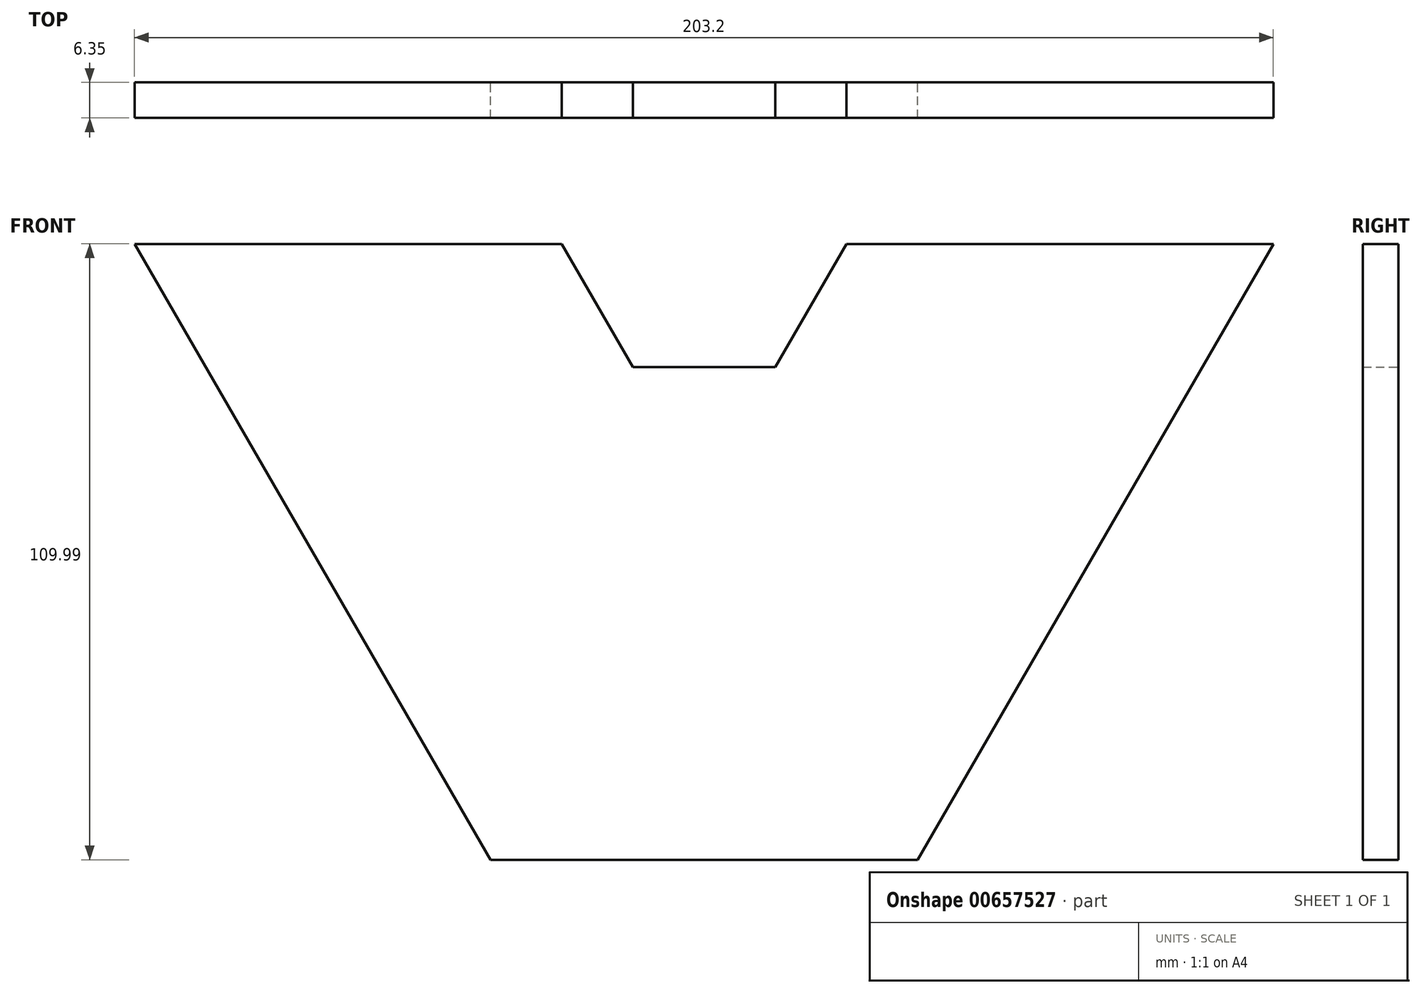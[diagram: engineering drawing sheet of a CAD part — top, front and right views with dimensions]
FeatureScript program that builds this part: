
annotation { "Feature Type Name" : "Feature", "Feature Type Description" : "" }
export const myFeature = defineFeature(function(context is Context, id is Id, definition is map)
    precondition{}
    {
        {
            var Q0;
            Q0=qCreatedBy(makeId("Front.planeOp"),FACE);
            var sketch = newSketch(context, id + "F0", { "sketchPlane" : qUnion([Q0])});
            skLineSegment(sketch, "E0", {"start": v(-34.47, 0) * mm, "end": v(41.73, 0) * mm});
            skLineSegment(sketch, "E1", {"start": v(41.73, 0) * mm, "end": v(105.23, 109.99) * mm});
            skLineSegment(sketch, "E2", {"start": v(105.23, 109.99) * mm, "end": v(29.03, 109.99) * mm});
            skLineSegment(sketch, "E3", {"start": v(29.03, 109.99) * mm, "end": v(16.33, 87.99) * mm});
            skLineSegment(sketch, "E4", {"start": v(16.33, 87.99) * mm, "end": v(-9.07, 87.99) * mm});
            skLineSegment(sketch, "E5", {"start": v(-9.07, 87.99) * mm, "end": v(-21.77, 109.99) * mm});
            skLineSegment(sketch, "E6", {"start": v(-21.77, 109.99) * mm, "end": v(-97.97, 109.99) * mm});
            skLineSegment(sketch, "E7", {"start": v(-97.97, 109.99) * mm, "end": v(-34.47, 0) * mm});
            skSolve(sketch);
        }
        {
            var Q0;
            Q0=makeQuery(id+"F0.imprint","IMPRINT",FACE,{"disambiguationData":[TD([[makeQuery(id+"F0.imprint","IMPRINT",EDGE,{"derivedFrom":sQuery(id+"F0.wireOp",EDGE,"E0")}),1.0]])]});
            extrude(context, id + "F1", {"entities" : qUnion([Q0]), "depth" : 6.35 * mm, "offsetDistance" : 25.4 * mm});
        }
    });
